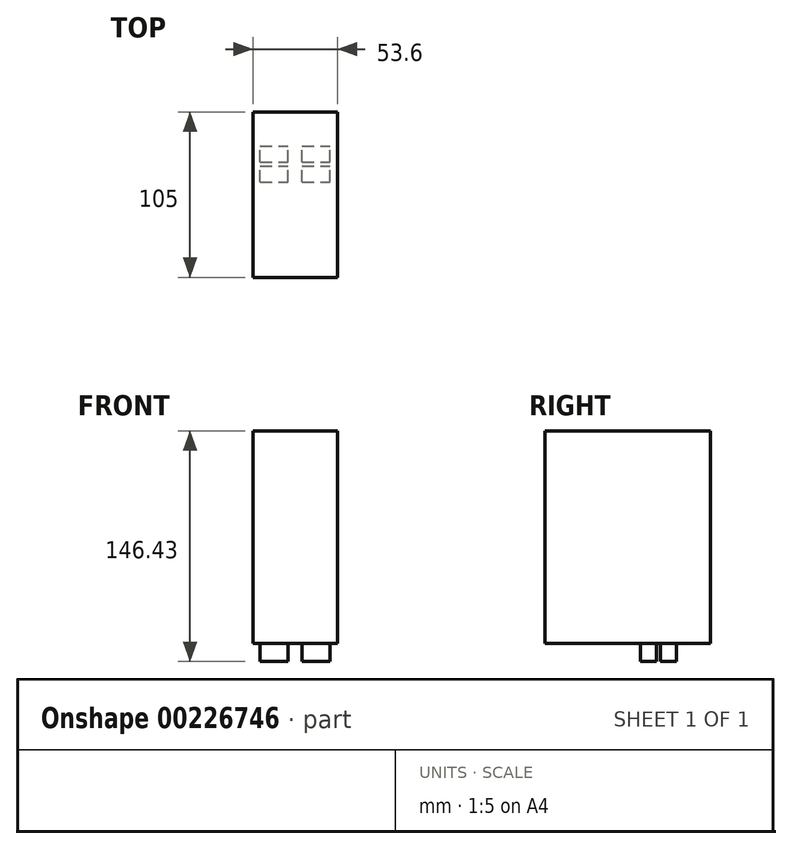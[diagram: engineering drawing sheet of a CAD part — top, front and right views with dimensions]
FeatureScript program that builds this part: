
annotation { "Feature Type Name" : "Feature", "Feature Type Description" : "" }
export const myFeature = defineFeature(function(context is Context, id is Id, definition is map)
    precondition{}
    {
        {
            var Q0;
            Q0=qCreatedBy(makeId("Front.planeOp"),FACE);
            var sketch = newSketch(context, id + "F0", { "sketchPlane" : qUnion([Q0])});
            skLineSegment(sketch, "E0.bottom", {"start": v(-26.8, 67.5) * mm, "end": v(26.8, 67.5) * mm});
            skLineSegment(sketch, "E0.top", {"start": v(-26.8, -67.5) * mm, "end": v(26.8, -67.5) * mm});
            skLineSegment(sketch, "E0.left", {"start": v(-26.8, 67.5) * mm, "end": v(-26.8, -67.5) * mm});
            skLineSegment(sketch, "E0.right", {"start": v(26.8, 67.5) * mm, "end": v(26.8, -67.5) * mm});
            skPoint(sketch, "E0.middle", {"position": v(0, 0) * mm});
            skSolve(sketch);
        }
        {
            var Q0;
            Q0=makeQuery(id+"F0.imprint","IMPRINT",FACE,{"disambiguationData":[TD([[makeQuery(id+"F0.imprint","IMPRINT",EDGE,{"derivedFrom":sQuery(id+"F0.wireOp",EDGE,"E0.bottom")}),-1.0]])]});
            extrude(context, id + "F1", {"entities" : qUnion([Q0]), "depth" : 105 * mm});
        }
        {
            var Q0;
            Q0=makeQuery(id+"F1.opExtrude","SWEPT_FACE",FACE,{"disambiguationData":[OSD([sQuery(id+"F0.wireOp",EDGE,"E0.top")])]});
            var sketch = newSketch(context, id + "F2", { "sketchPlane" : qUnion([Q0])});
            skLineSegment(sketch, "E1.bottom", {"start": v(4.45, 31.75) * mm, "end": v(22.23, 31.75) * mm});
            skLineSegment(sketch, "E1.top", {"start": v(4.45, 21.59) * mm, "end": v(22.23, 21.59) * mm});
            skLineSegment(sketch, "E1.left", {"start": v(4.45, 31.75) * mm, "end": v(4.45, 21.59) * mm});
            skLineSegment(sketch, "E1.right", {"start": v(22.23, 31.75) * mm, "end": v(22.23, 21.6) * mm});
            skLineSegment(sketch, "E2.0.1.0", {"start": v(22.23, 44.45) * mm, "end": v(22.23, 34.29) * mm});
            skLineSegment(sketch, "E2.0.1.1", {"start": v(4.45, 44.45) * mm, "end": v(4.45, 34.29) * mm});
            skLineSegment(sketch, "E2.0.1.2", {"start": v(4.45, 44.45) * mm, "end": v(22.23, 44.45) * mm});
            skLineSegment(sketch, "E2.0.1.3", {"start": v(4.45, 34.3) * mm, "end": v(22.23, 34.3) * mm});
            skLineSegment(sketch, "E2.1.0.0", {"start": v(-4.44, 31.75) * mm, "end": v(-4.44, 21.59) * mm});
            skLineSegment(sketch, "E2.1.0.1", {"start": v(-22.22, 31.75) * mm, "end": v(-22.22, 21.59) * mm});
            skLineSegment(sketch, "E2.1.0.2", {"start": v(-22.22, 31.75) * mm, "end": v(-4.44, 31.75) * mm});
            skLineSegment(sketch, "E2.1.0.3", {"start": v(-22.22, 21.59) * mm, "end": v(-4.44, 21.59) * mm});
            skLineSegment(sketch, "E2.1.1.0", {"start": v(-4.44, 44.45) * mm, "end": v(-4.44, 34.29) * mm});
            skLineSegment(sketch, "E2.1.1.1", {"start": v(-22.22, 44.45) * mm, "end": v(-22.22, 34.29) * mm});
            skLineSegment(sketch, "E2.1.1.2", {"start": v(-22.22, 44.45) * mm, "end": v(-4.44, 44.45) * mm});
            skLineSegment(sketch, "E2.1.1.3", {"start": v(-22.22, 34.3) * mm, "end": v(-4.44, 34.3) * mm});
            skLineSegment(sketch, "E2.direction1", {"start": v(4.45, 21.59) * mm, "end": v(-22.22, 21.59) * mm, "construction": true});
            skLineSegment(sketch, "E2.direction2", {"start": v(4.45, 21.59) * mm, "end": v(4.45, 34.29) * mm, "construction": true});
            skSolve(sketch);
        }
        {
            var Q0;
            Q0=makeQuery(id+"F2.imprint","IMPRINT",FACE,{"disambiguationData":[TD([[makeQuery(id+"F2.imprint","IMPRINT",EDGE,{"derivedFrom":sQuery(id+"F2.wireOp",EDGE,"E1.bottom")}),-1.0]])]});
            var Q1;
            Q1=makeQuery(id+"F2.imprint","IMPRINT",FACE,{"disambiguationData":[TD([[makeQuery(id+"F2.imprint","IMPRINT",EDGE,{"derivedFrom":sQuery(id+"F2.wireOp",EDGE,"E2.0.1.0")}),-1.0]])]});
            var Q2;
            Q2=makeQuery(id+"F2.imprint","IMPRINT",FACE,{"disambiguationData":[TD([[makeQuery(id+"F2.imprint","IMPRINT",EDGE,{"derivedFrom":sQuery(id+"F2.wireOp",EDGE,"E2.1.1.0")}),-1.0]])]});
            var Q3;
            Q3=makeQuery(id+"F2.imprint","IMPRINT",FACE,{"disambiguationData":[TD([[makeQuery(id+"F2.imprint","IMPRINT",EDGE,{"derivedFrom":sQuery(id+"F2.wireOp",EDGE,"E2.1.0.0")}),-1.0]])]});
            extrude(context, id + "F3", {"entities" : qUnion([Q0, Q1, Q2, Q3]), "operationType" : NewBodyOperationType.ADD, "depth" : 11.43 * mm});
        }
    });
